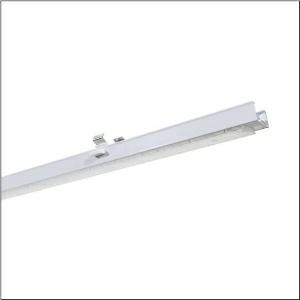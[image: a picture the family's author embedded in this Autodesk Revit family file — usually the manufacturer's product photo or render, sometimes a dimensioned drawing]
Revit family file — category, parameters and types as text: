
# Revit family: trunking_flex_31_51re12db4cb
name_source: partatom
category: Lighting Fixtures
units: mm (PartAtom-declared; Revit-internal decimal feet)

## family parameters
Cut with Voids When Loaded = No
Host = Face
Light Source = No
Part Type = Normal
Room Calculation Point = No
Round Connector Dimension = Use Diameter
Shared = No

## types (1)
- Trunking Flex 31 (1 x LED, 11500 lm, 66 W, 4000K)
    Apparent Load = 66 VA
    CIE Flux Codes = 65 91 98 99 100
    Color Rendering = 80
    Color Temperature = 4000K
    Default Elevation = 1800 mm
    Description = Trunking Flex 31, luminaire insert, of extruded aluminium section, coated, traffic white (RAL 9016), length: 1.472mm, width: 91mm, height: 53mm, LED rated luminous flux: 11.500lm, light colour: 840, control gear: DALI 2, with system connector: socket, mains connection: 220..240V, AC, 50/60Hz, rated input power: 66W, primary light control with lens, of plastic, primary optical cover: cover, of PMMA, light emission: direct distribution, protection rating (complete): IP20, insulation class (complete): insulation class I (protective earthing), certification: CE, UKCA, impact resistance: IK02, permissible ambient temperature for indoor applications: -20..+40°C, packaging unit: 1 piece
    Height = 58 mm
    Lamp = 1 x LED
    Lamp Light Flux = 11500 lm
    Lamp Power = 66 W
    Lamp count = 1
    Length = 1472 mm
    Luminous efficacy = 174 lm/W
    Manufacturer = Siteco
    ModVariant = No
    Model = 51RE12DB4CB
    Mounting Place = Ceiling
    Mounting Type = Pendant
    Number of Poles = 1
    OnlyDefault = Yes
    Power Factor = 1
    Product Name = Trunking Flex 31
    Product group = luminaire insert
    ProductGroupID = 902
    Protection Class = Protection class I
    Protection Degree = IP 20
    RLX_Detail_Level = 1
    RLX_Emergency_Light_Flux = 0 lm
    RLX_Emergency_Type = 0
    RLX_Emergency_Type_DB = No
    RlxData = <blob elided: 19553 chars, md5=763d9099>
    Socket = socket
    Standby Power = 0 W
    System Light Flux = 11500 lm
    System Power = 66 W
    Type Comments = Product without accessories
    Type Image = l_1266702.jpg
    URL = http://relux.com
    VarID = ---
    Voltage = 0 V
    Weight = 0.00 kg
    Width = 65 mm

## geometry (parser evidence)
native form markers: Blend x4, Sweep x10
no freeform markers — native parametric forms only
